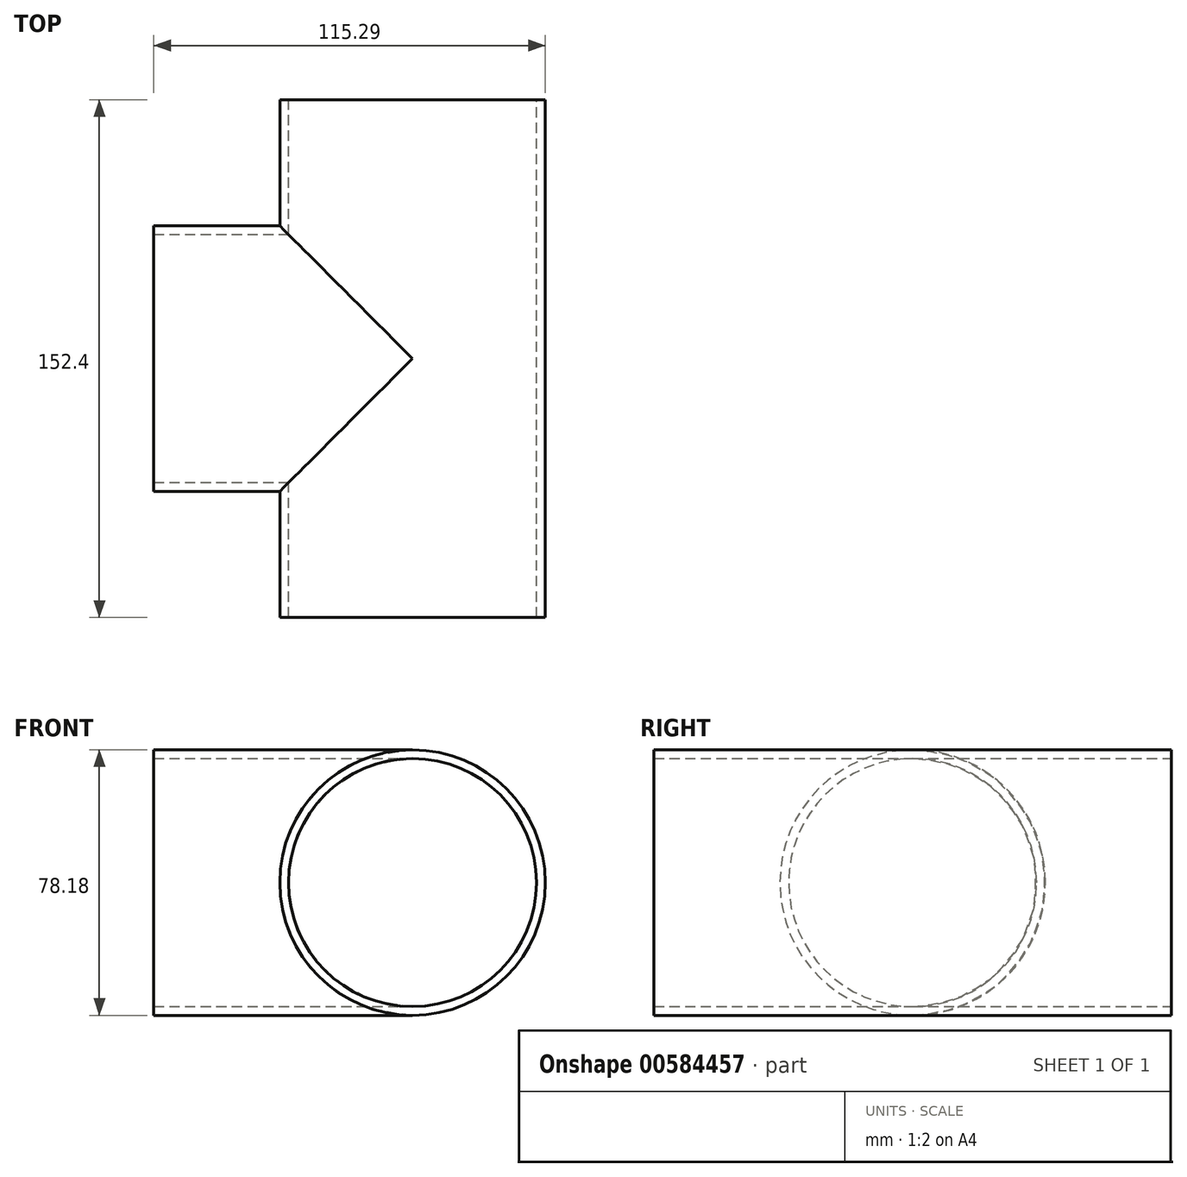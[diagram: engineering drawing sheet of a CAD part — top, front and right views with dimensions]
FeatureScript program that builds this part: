
annotation { "Feature Type Name" : "Feature", "Feature Type Description" : "" }
export const myFeature = defineFeature(function(context is Context, id is Id, definition is map)
    precondition{}
    {
        {
            var Q0;
            Q0=qCreatedBy(makeId("Front.planeOp"),FACE);
            var sketch = newSketch(context, id + "F0", { "sketchPlane" : qUnion([Q0])});
            skCircle(sketch, "E0", {"center": v(0, 0) * mm, "radius": 36.51 * mm});
            skCircle(sketch, "E1", {"center": v(0, 0) * mm, "radius": 39.1 * mm});
            skSolve(sketch);
        }
        {
            var Q0;
            Q0=qCreatedBy(makeId("Right.planeOp"),FACE);
            var sketch = newSketch(context, id + "F1", { "sketchPlane" : qUnion([Q0])});
            skLineSegment(sketch, "E2", {"start": v(0, 0) * mm, "end": v(152.4, 0) * mm});
            skSolve(sketch);
        }
        {
            var Q0;
            Q0=makeQuery(id+"F0.imprint","IMPRINT",FACE,{"disambiguationData":[TD([[makeQuery(id+"F0.imprint","IMPRINT",EDGE,{"derivedFrom":sQuery(id+"F0.wireOp",EDGE,"E0")}),-1.0]])]});
            var Q1;
            Q1=sQuery(id+"F1.wireOp",EDGE,"E2");
            sweep(context, id + "F2", {"profiles" : qUnion([Q0]), "path" : qUnion([Q1])});
        }
        {
            var Q0;
            Q0=qCreatedBy(makeId("Right.planeOp"),FACE);
            var sketch = newSketch(context, id + "F3", { "sketchPlane" : qUnion([Q0])});
            skLineSegment(sketch, "E3.bottom", {"start": v(152.4, -39.1) * mm, "end": v(0, -39.1) * mm, "construction": true});
            skLineSegment(sketch, "E3.left", {"start": v(152.4, -39.1) * mm, "end": v(152.4, 39.1) * mm, "construction": true});
            skPoint(sketch, "E3.middle", {"position": v(0, 0) * mm});
            skLineSegment(sketch, "E4", {"start": v(0, -39.1) * mm, "end": v(0, 39.1) * mm, "construction": true});
            skPoint(sketch, "E3.right.end.orphan", {"position": v(-152.4, 39.1) * mm});
            skPoint(sketch, "E3.right.start.orphan", {"position": v(-152.4, -39.1) * mm});
            skLineSegment(sketch, "E5", {"start": v(0, 0) * mm, "end": v(152.4, 0) * mm, "construction": true});
            skCircle(sketch, "E6", {"center": v(76.2, 0) * mm, "radius": 36.51 * mm});
            skSolve(sketch);
        }
        {
            var Q0;
            Q0=qSketchRegion(id+"F3",true);
            extrude(context, id + "F4", {"entities" : qUnion([Q0]), "operationType" : NewBodyOperationType.REMOVE, "oppositeDirection" : true, "depth" : 47.5 * mm, "offsetDistance" : 25.4 * mm});
        }
        {
            var Q0;
            Q0=qCreatedBy(makeId("Right.planeOp"),FACE);
            var sketch = newSketch(context, id + "F5", { "sketchPlane" : qUnion([Q0])});
            skLineSegment(sketch, "E7.bottom", {"start": v(152.4, -39.1) * mm, "end": v(0, -39.1) * mm, "construction": true});
            skLineSegment(sketch, "E7.top", {"start": v(152.4, 39.1) * mm, "end": v(0, 39.1) * mm, "construction": true});
            skLineSegment(sketch, "E7.left", {"start": v(152.4, -39.1) * mm, "end": v(152.4, 39.1) * mm, "construction": true});
            skPoint(sketch, "E7.middle", {"position": v(0, 0) * mm});
            skLineSegment(sketch, "E8", {"start": v(0, -39.1) * mm, "end": v(0, 39.1) * mm, "construction": true});
            skPoint(sketch, "E7.right.start.orphan", {"position": v(-152.4, -39.1) * mm});
            skPoint(sketch, "E9.orphan", {"position": v(-152.4, 39.1) * mm});
            skLineSegment(sketch, "E10", {"start": v(0, 0) * mm, "end": v(152.4, 0) * mm, "construction": true});
            skCircle(sketch, "E11", {"center": v(76.2, 0) * mm, "radius": 36.51 * mm});
            skCircle(sketch, "E12", {"center": v(76.2, 0) * mm, "radius": 39.1 * mm});
            skSolve(sketch);
        }
        {
            var Q0;
            Q0=qSketchRegion(id+"F5",true);
            extrude(context, id + "F6", {"entities" : qUnion([Q0]), "operationType" : NewBodyOperationType.ADD, "oppositeDirection" : true, "depth" : 76.2 * mm, "offsetDistance" : 25.4 * mm});
        }
        {
            var Q0;
            Q0=qCreatedBy(makeId("Front.planeOp"),FACE);
            var sketch = newSketch(context, id + "F7", { "sketchPlane" : qUnion([Q0])});
            skCircle(sketch, "E13", {"center": v(0, 0) * mm, "radius": 36.51 * mm});
            skSolve(sketch);
        }
        {
            var Q0;
            Q0=qSketchRegion(id+"F7",true);
            extrude(context, id + "F8", {"entities" : qUnion([Q0]), "operationType" : NewBodyOperationType.REMOVE, "oppositeDirection" : true, "depth" : 156.72 * mm, "offsetDistance" : 25.4 * mm});
        }
    });
